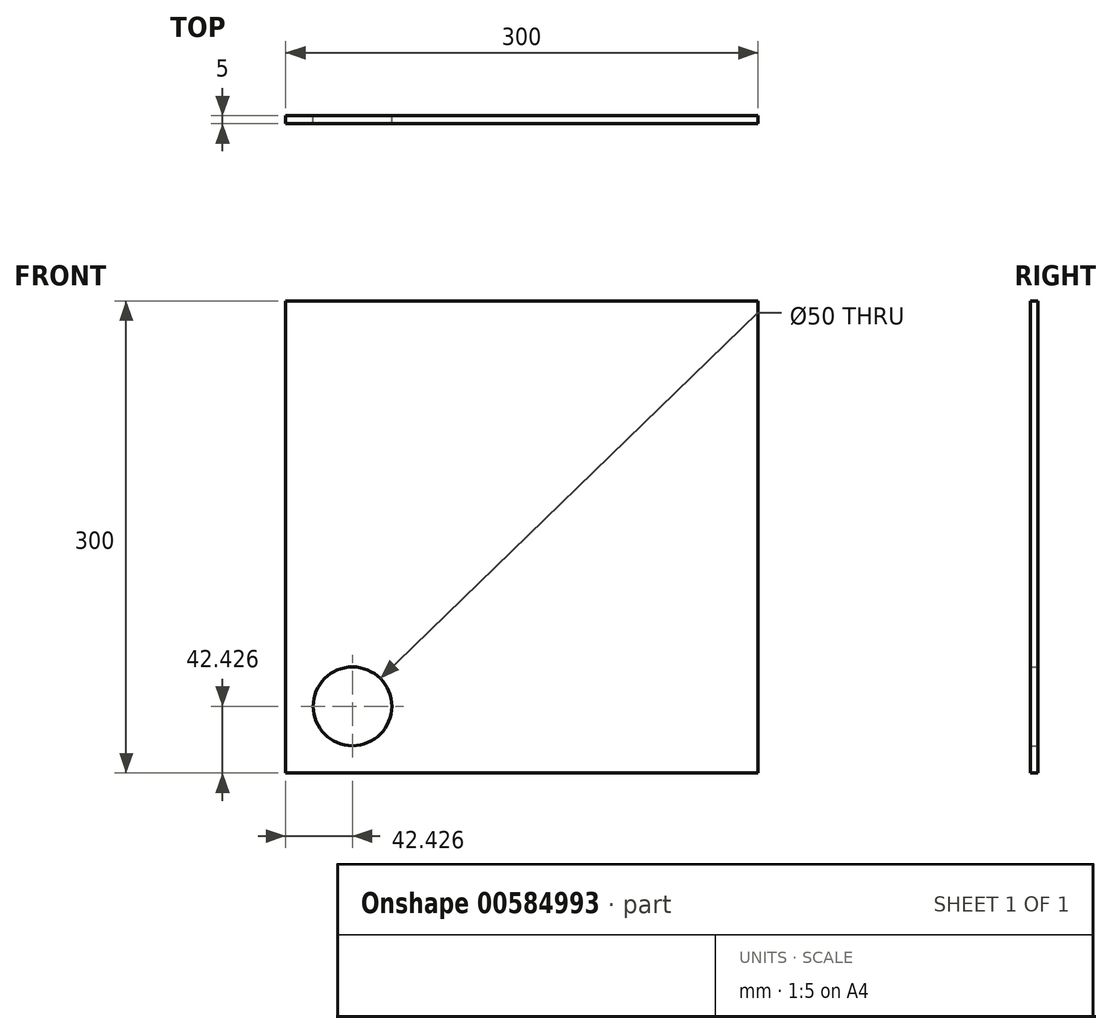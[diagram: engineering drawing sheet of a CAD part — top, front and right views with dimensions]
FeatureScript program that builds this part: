
annotation { "Feature Type Name" : "Feature", "Feature Type Description" : "" }
export const myFeature = defineFeature(function(context is Context, id is Id, definition is map)
    precondition{}
    {
        {
            var Q0;
            Q0=qCreatedBy(makeId("Front.planeOp"),FACE);
            var sketch = newSketch(context, id + "F0", { "sketchPlane" : qUnion([Q0])});
            skLineSegment(sketch, "E0.bottom", {"start": v(150, 150) * mm, "end": v(-150, 150) * mm});
            skLineSegment(sketch, "E0.top", {"start": v(150, -150) * mm, "end": v(-150, -150) * mm});
            skLineSegment(sketch, "E0.left", {"start": v(150, 150) * mm, "end": v(150, -150) * mm});
            skLineSegment(sketch, "E0.right", {"start": v(-150, 150) * mm, "end": v(-150, -150) * mm});
            skPoint(sketch, "E0.middle", {"position": v(0, 0) * mm});
            skCircle(sketch, "E1", {"center": v(-107.57, -107.57) * mm, "radius": 25 * mm});
            skSolve(sketch);
        }
        {
            var Q0;
            Q0 = qSketchRegion(id + "F0", true);
            extrude(context, id + "F1", {"entities" : qUnion([Q0]), "depth" : 5 * mm, "offsetDistance" : 25 * mm});
        }
    });
